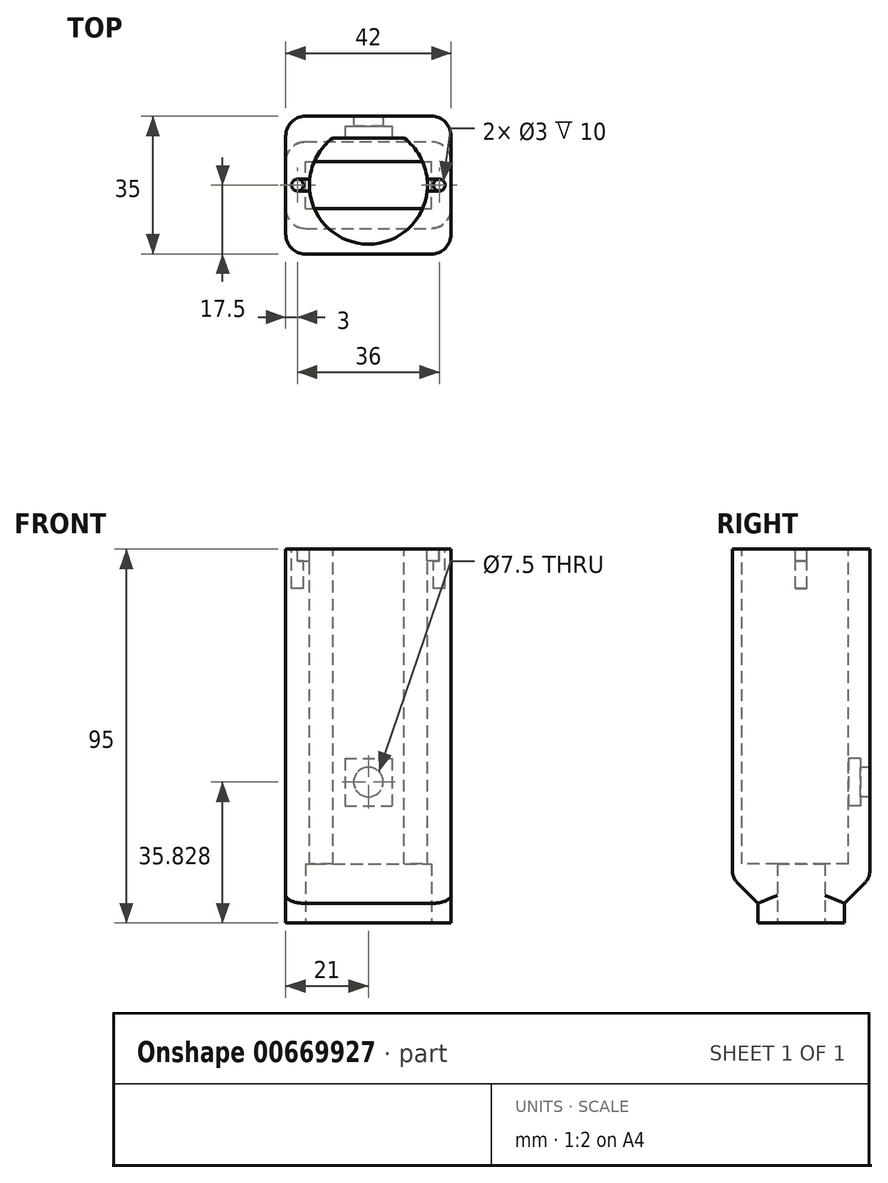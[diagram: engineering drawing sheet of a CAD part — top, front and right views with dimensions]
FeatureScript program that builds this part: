
annotation { "Feature Type Name" : "Feature", "Feature Type Description" : "" }
export const myFeature = defineFeature(function(context is Context, id is Id, definition is map)
    precondition{}
    {
        {
            var Q0;
            Q0=qCreatedBy(makeId("Top.planeOp"),FACE);
            var sketch = newSketch(context, id + "F0", { "sketchPlane" : qUnion([Q0])});
            skLineSegment(sketch, "E0.bottom", {"start": v(-21, 11) * mm, "end": v(21, 11) * mm});
            skLineSegment(sketch, "E0.top", {"start": v(-21, -11) * mm, "end": v(21, -11) * mm});
            skLineSegment(sketch, "E0.left", {"start": v(-21, 11) * mm, "end": v(-21, -11) * mm});
            skLineSegment(sketch, "E0.right", {"start": v(21, 11) * mm, "end": v(21, -11) * mm});
            skSolve(sketch);
        }
        {
            var Q0;
            Q0 = qSketchRegion(id + "F0", true);
            extrude(context, id + "F1", {"entities" : qUnion([Q0]), "oppositeDirection" : true, "depth" : 5 * mm, "offsetDistance" : 25 * mm});
        }
        {
            var Q0;
            Q0=qCreatedBy(makeId("Top.planeOp"),FACE);
            var sketch = newSketch(context, id + "F2", { "sketchPlane" : qUnion([Q0])});
            skLineSegment(sketch, "E1.bottom", {"start": v(-21, 17.5) * mm, "end": v(21, 17.5) * mm});
            skLineSegment(sketch, "E1.top", {"start": v(-21, -17.5) * mm, "end": v(21, -17.5) * mm});
            skLineSegment(sketch, "E1.left", {"start": v(-21, 17.5) * mm, "end": v(-21, -17.5) * mm});
            skLineSegment(sketch, "E1.right", {"start": v(21, 17.5) * mm, "end": v(21, -17.5) * mm});
            skSolve(sketch);
        }
        {
            var Q0;
            Q0 = qSketchRegion(id + "F2", true);
            extrude(context, id + "F3", {"entities" : qUnion([Q0]), "operationType" : NewBodyOperationType.ADD, "depth" : 90 * mm, "offsetDistance" : 25 * mm});
        }
        {
            var Q0;
            Q0=makeQuery(id+"F3.opExtrude","CAP_EDGE",EDGE,{"disambiguationData":[OSD([sQuery(id+"F2.wireOp",EDGE,"E1.top")])],"isStart":true});
            var Q1;
            Q1=makeQuery(id+"F3.opExtrude","CAP_EDGE",EDGE,{"disambiguationData":[OSD([sQuery(id+"F2.wireOp",EDGE,"E1.bottom")])],"isStart":true});
            chamfer(context, id + "F4", {"entities" : qUnion([Q0, Q1]), "width" : 6.5 * mm, "tangentPropagation" : true});
        }
        {
            var Q0;
            Q0=makeQuery(id+"F3.opExtrude","CAP_FACE",FACE,{"disambiguationData":[OSD([sQuery(id+"F2.wireOp",EDGE,"E1.bottom"),sQuery(id+"F2.wireOp",EDGE,"E1.top"),sQuery(id+"F2.wireOp",EDGE,"E1.left"),sQuery(id+"F2.wireOp",EDGE,"E1.right")])],"isStart":false});
            var sketch = newSketch(context, id + "F5", { "sketchPlane" : qUnion([Q0])});
            skCircle(sketch, "E2", {"center": v(0, 0) * mm, "radius": 15 * mm});
            skLineSegment(sketch, "E3", {"start": v(-9, 12) * mm, "end": v(9, 12) * mm});
            skSolve(sketch);
        }
        {
            var Q0;
            {var subQ0=sQuery(id+"F5.wireOp",EDGE,"E3");Q0=makeQuery(id+"F5.imprint","IMPRINT",FACE,{"disambiguationData":[TD([[makeQuery(id+"F5.imprint","IMPRINT",EDGE,{"derivedFrom":subQ0}),-1.0]])]});}
            extrude(context, id + "F6", {"entities" : qUnion([Q0]), "operationType" : NewBodyOperationType.REMOVE, "oppositeDirection" : true, "depth" : 80 * mm, "offsetDistance" : 25 * mm});
        }
        {
            var Q0;
            Q0=makeQuery(id+"F3.opExtrude","SWEPT_EDGE",EDGE,{"disambiguationData":[OSD([sQuery(id+"F2.wireOp",EDGE,"E1.top"),sQuery(id+"F2.wireOp",EDGE,"E1.right")])]});
            var Q1;
            Q1=makeQuery(id+"F4.opChamfer","BLEND_EDGE",EDGE,{"blendedFrom":[makeQuery(id+"F3.opExtrude","CAP_EDGE",EDGE,{"disambiguationData":[OSD([sQuery(id+"F2.wireOp",EDGE,"E1.top")])],"isStart":true}),makeQuery(id+"F3.boolean.opBoolean","MERGE",FACE,{"derivedFrom":[makeQuery(id+"F1.opExtrude","SWEPT_FACE",FACE,{"disambiguationData":[OSD([sQuery(id+"F0.wireOp",EDGE,"E0.right")])]}),makeQuery(id+"F3.opExtrude","SWEPT_FACE",FACE,{"disambiguationData":[OSD([sQuery(id+"F2.wireOp",EDGE,"E1.right")])]})]})],"blendedInto":[makeQuery(id+"F3.boolean.opBoolean","MERGE",FACE,{"derivedFrom":[makeQuery(id+"F1.opExtrude","SWEPT_FACE",FACE,{"disambiguationData":[OSD([sQuery(id+"F0.wireOp",EDGE,"E0.right")])]}),makeQuery(id+"F3.opExtrude","SWEPT_FACE",FACE,{"disambiguationData":[OSD([sQuery(id+"F2.wireOp",EDGE,"E1.right")])]})]})]});
            var Q2;
            Q2=makeQuery(id+"F1.opExtrude","SWEPT_EDGE",EDGE,{"disambiguationData":[OSD([sQuery(id+"F0.wireOp",EDGE,"E0.top"),sQuery(id+"F0.wireOp",EDGE,"E0.right")])]});
            var Q3;
            Q3=makeQuery(id+"F3.opExtrude","SWEPT_EDGE",EDGE,{"disambiguationData":[OSD([sQuery(id+"F2.wireOp",EDGE,"E1.top"),sQuery(id+"F2.wireOp",EDGE,"E1.left")])]});
            var Q4;
            Q4=makeQuery(id+"F4.opChamfer","BLEND_EDGE",EDGE,{"blendedFrom":[makeQuery(id+"F3.opExtrude","CAP_EDGE",EDGE,{"disambiguationData":[OSD([sQuery(id+"F2.wireOp",EDGE,"E1.top")])],"isStart":true}),makeQuery(id+"F3.boolean.opBoolean","MERGE",FACE,{"derivedFrom":[makeQuery(id+"F1.opExtrude","SWEPT_FACE",FACE,{"disambiguationData":[OSD([sQuery(id+"F0.wireOp",EDGE,"E0.left")])]}),makeQuery(id+"F3.opExtrude","SWEPT_FACE",FACE,{"disambiguationData":[OSD([sQuery(id+"F2.wireOp",EDGE,"E1.left")])]})]})],"blendedInto":[makeQuery(id+"F3.boolean.opBoolean","MERGE",FACE,{"derivedFrom":[makeQuery(id+"F1.opExtrude","SWEPT_FACE",FACE,{"disambiguationData":[OSD([sQuery(id+"F0.wireOp",EDGE,"E0.left")])]}),makeQuery(id+"F3.opExtrude","SWEPT_FACE",FACE,{"disambiguationData":[OSD([sQuery(id+"F2.wireOp",EDGE,"E1.left")])]})]})]});
            var Q5;
            Q5=makeQuery(id+"F1.opExtrude","SWEPT_EDGE",EDGE,{"disambiguationData":[OSD([sQuery(id+"F0.wireOp",EDGE,"E0.top"),sQuery(id+"F0.wireOp",EDGE,"E0.left")])]});
            var Q6;
            Q6=makeQuery(id+"F3.opExtrude","SWEPT_EDGE",EDGE,{"disambiguationData":[OSD([sQuery(id+"F2.wireOp",EDGE,"E1.bottom"),sQuery(id+"F2.wireOp",EDGE,"E1.left")])]});
            var Q7;
            Q7=makeQuery(id+"F4.opChamfer","BLEND_EDGE",EDGE,{"blendedFrom":[makeQuery(id+"F3.opExtrude","CAP_EDGE",EDGE,{"disambiguationData":[OSD([sQuery(id+"F2.wireOp",EDGE,"E1.bottom")])],"isStart":true}),makeQuery(id+"F3.boolean.opBoolean","MERGE",FACE,{"derivedFrom":[makeQuery(id+"F1.opExtrude","SWEPT_FACE",FACE,{"disambiguationData":[OSD([sQuery(id+"F0.wireOp",EDGE,"E0.left")])]}),makeQuery(id+"F3.opExtrude","SWEPT_FACE",FACE,{"disambiguationData":[OSD([sQuery(id+"F2.wireOp",EDGE,"E1.left")])]})]})],"blendedInto":[makeQuery(id+"F3.boolean.opBoolean","MERGE",FACE,{"derivedFrom":[makeQuery(id+"F1.opExtrude","SWEPT_FACE",FACE,{"disambiguationData":[OSD([sQuery(id+"F0.wireOp",EDGE,"E0.left")])]}),makeQuery(id+"F3.opExtrude","SWEPT_FACE",FACE,{"disambiguationData":[OSD([sQuery(id+"F2.wireOp",EDGE,"E1.left")])]})]})]});
            var Q8;
            Q8=makeQuery(id+"F1.opExtrude","SWEPT_EDGE",EDGE,{"disambiguationData":[OSD([sQuery(id+"F0.wireOp",EDGE,"E0.bottom"),sQuery(id+"F0.wireOp",EDGE,"E0.left")])]});
            var Q9;
            Q9=makeQuery(id+"F3.opExtrude","SWEPT_EDGE",EDGE,{"disambiguationData":[OSD([sQuery(id+"F2.wireOp",EDGE,"E1.bottom"),sQuery(id+"F2.wireOp",EDGE,"E1.right")])]});
            var Q10;
            Q10=makeQuery(id+"F4.opChamfer","BLEND_EDGE",EDGE,{"blendedFrom":[makeQuery(id+"F3.opExtrude","CAP_EDGE",EDGE,{"disambiguationData":[OSD([sQuery(id+"F2.wireOp",EDGE,"E1.bottom")])],"isStart":true}),makeQuery(id+"F3.boolean.opBoolean","MERGE",FACE,{"derivedFrom":[makeQuery(id+"F1.opExtrude","SWEPT_FACE",FACE,{"disambiguationData":[OSD([sQuery(id+"F0.wireOp",EDGE,"E0.right")])]}),makeQuery(id+"F3.opExtrude","SWEPT_FACE",FACE,{"disambiguationData":[OSD([sQuery(id+"F2.wireOp",EDGE,"E1.right")])]})]})],"blendedInto":[makeQuery(id+"F3.boolean.opBoolean","MERGE",FACE,{"derivedFrom":[makeQuery(id+"F1.opExtrude","SWEPT_FACE",FACE,{"disambiguationData":[OSD([sQuery(id+"F0.wireOp",EDGE,"E0.right")])]}),makeQuery(id+"F3.opExtrude","SWEPT_FACE",FACE,{"disambiguationData":[OSD([sQuery(id+"F2.wireOp",EDGE,"E1.right")])]})]})]});
            var Q11;
            Q11=makeQuery(id+"F1.opExtrude","SWEPT_EDGE",EDGE,{"disambiguationData":[OSD([sQuery(id+"F0.wireOp",EDGE,"E0.bottom"),sQuery(id+"F0.wireOp",EDGE,"E0.right")])]});
            var Q12;
            {var subQ0=sQuery(id+"F2.wireOp",EDGE,"E1.bottom");Q12=makeQuery(id+"F4.opChamfer","BLEND_EDGE",EDGE,{"blendedFrom":[makeQuery(id+"F3.opExtrude","CAP_EDGE",EDGE,{"disambiguationData":[OSD([subQ0])],"isStart":true}),makeQuery(id+"F3.opExtrude","SWEPT_FACE",FACE,{"disambiguationData":[OSD([subQ0])]})],"blendedInto":[makeQuery(id+"F3.opExtrude","SWEPT_FACE",FACE,{"disambiguationData":[OSD([subQ0])]})]});}
            var Q13;
            {var subQ0=sQuery(id+"F2.wireOp",EDGE,"E1.top");Q13=makeQuery(id+"F4.opChamfer","BLEND_EDGE",EDGE,{"blendedFrom":[makeQuery(id+"F3.opExtrude","CAP_EDGE",EDGE,{"disambiguationData":[OSD([subQ0])],"isStart":true}),makeQuery(id+"F3.opExtrude","SWEPT_FACE",FACE,{"disambiguationData":[OSD([subQ0])]})],"blendedInto":[makeQuery(id+"F3.opExtrude","SWEPT_FACE",FACE,{"disambiguationData":[OSD([subQ0])]})]});}
            fillet(context, id + "F7", {"entities" : qUnion([Q0, Q1, Q2, Q3, Q4, Q5, Q6, Q7, Q8, Q9, Q10, Q11, Q12, Q13]), "radius" : 5 * mm, "tangentPropagation" : true, "allowEdgeOverflow" : false});
        }
        {
            var Q0;
            Q0=makeQuery(id+"F1.opExtrude","CAP_FACE",FACE,{"disambiguationData":[OSD([sQuery(id+"F0.wireOp",EDGE,"E0.bottom"),sQuery(id+"F0.wireOp",EDGE,"E0.top"),sQuery(id+"F0.wireOp",EDGE,"E0.left"),sQuery(id+"F0.wireOp",EDGE,"E0.right")])],"isStart":false});
            var sketch = newSketch(context, id + "F8", { "sketchPlane" : qUnion([Q0])});
            skLineSegment(sketch, "E4.bottom", {"start": v(-16, 6) * mm, "end": v(16, 6) * mm});
            skLineSegment(sketch, "E4.top", {"start": v(-16, -6) * mm, "end": v(16, -6) * mm});
            skLineSegment(sketch, "E4.left", {"start": v(-16, 6) * mm, "end": v(-16, -6) * mm});
            skLineSegment(sketch, "E4.right", {"start": v(16, 6) * mm, "end": v(16, -6) * mm});
            skSolve(sketch);
        }
        {
            var Q0;
            Q0 = qSketchRegion(id + "F8", true);
            extrude(context, id + "F9", {"entities" : qUnion([Q0]), "operationType" : NewBodyOperationType.REMOVE, "oppositeDirection" : true, "depth" : 15 * mm, "offsetDistance" : 25 * mm});
        }
        {
            var Q0;
            Q0=makeQuery(id+"F6.boolean.opBoolean","COPY",FACE,{"derivedFrom":makeQuery(id+"F6.opExtrude","SWEPT_FACE",FACE,{"disambiguationData":[OSD([sQuery(id+"F5.wireOp",EDGE,"E3")])]})});
            var sketch = newSketch(context, id + "F10", { "sketchPlane" : qUnion([Q0])});
            skLineSegment(sketch, "E5.bottom", {"start": v(-6, 36.83) * mm, "end": v(6, 36.83) * mm});
            skLineSegment(sketch, "E5.top", {"start": v(-6, 24.83) * mm, "end": v(6, 24.83) * mm});
            skLineSegment(sketch, "E5.left", {"start": v(-6, 36.83) * mm, "end": v(-6, 24.83) * mm});
            skLineSegment(sketch, "E5.right", {"start": v(6, 36.83) * mm, "end": v(6, 24.83) * mm});
            skCircle(sketch, "E6", {"center": v(0, 30.83) * mm, "radius": 3.75 * mm});
            skSolve(sketch);
        }
        {
            var Q0;
            Q0 = qSketchRegion(id + "F10", true);
            extrude(context, id + "F11", {"entities" : qUnion([Q0]), "operationType" : NewBodyOperationType.REMOVE, "oppositeDirection" : true, "depth" : 3 * mm, "offsetDistance" : 25 * mm});
        }
        {
            var Q0;
            Q0=makeQuery(id+"F11.boolean.opBoolean","SPLIT",FACE,{"disambiguationData":[TD([makeQuery(id+"F11.opExtrude","SWEPT_FACE",FACE,{"disambiguationData":[OSD([sQuery(id+"F10.wireOp",EDGE,"E6")])]})])],"derivedFrom":makeQuery(id+"F6.boolean.opBoolean","COPY",FACE,{"derivedFrom":makeQuery(id+"F6.opExtrude","SWEPT_FACE",FACE,{"disambiguationData":[OSD([sQuery(id+"F5.wireOp",EDGE,"E3")])]})})});
            extrude(context, id + "F12", {"entities" : qUnion([Q0]), "operationType" : NewBodyOperationType.REMOVE, "oppositeDirection" : true, "depth" : 10 * mm, "offsetDistance" : 25 * mm});
        }
        {
            var Q0;
            Q0=makeQuery(id+"F3.opExtrude","CAP_FACE",FACE,{"disambiguationData":[OSD([sQuery(id+"F2.wireOp",EDGE,"E1.bottom"),sQuery(id+"F2.wireOp",EDGE,"E1.top"),sQuery(id+"F2.wireOp",EDGE,"E1.left"),sQuery(id+"F2.wireOp",EDGE,"E1.right")])],"isStart":false});
            var sketch = newSketch(context, id + "F13", { "sketchPlane" : qUnion([Q0])});
            skCircle(sketch, "E7", {"center": v(-18, 0) * mm, "radius": 1.5 * mm});
            skCircle(sketch, "E8", {"center": v(18, 0) * mm, "radius": 1.5 * mm});
            skSolve(sketch);
        }
        {
            var Q0;
            Q0 = qSketchRegion(id + "F13", true);
            extrude(context, id + "F14", {"entities" : qUnion([Q0]), "operationType" : NewBodyOperationType.REMOVE, "oppositeDirection" : true, "depth" : 10 * mm, "offsetDistance" : 25 * mm});
        }
        {
            var Q0;
            Q0=makeQuery(id+"F3.opExtrude","CAP_FACE",FACE,{"disambiguationData":[OSD([sQuery(id+"F2.wireOp",EDGE,"E1.bottom"),sQuery(id+"F2.wireOp",EDGE,"E1.top"),sQuery(id+"F2.wireOp",EDGE,"E1.left"),sQuery(id+"F2.wireOp",EDGE,"E1.right")])],"isStart":false});
            var sketch = newSketch(context, id + "F15", { "sketchPlane" : qUnion([Q0])});
            skLineSegment(sketch, "E9.bottom", {"start": v(-17.95, 1.5) * mm, "end": v(-14.92, 1.5) * mm});
            skLineSegment(sketch, "E9.top", {"start": v(-17.95, -1.5) * mm, "end": v(-14.92, -1.5) * mm});
            skLineSegment(sketch, "E9.left", {"start": v(-17.95, 1.5) * mm, "end": v(-17.95, -1.5) * mm});
            skLineSegment(sketch, "E9.right", {"start": v(-14.92, 1.5) * mm, "end": v(-14.92, -1.5) * mm});
            skLineSegment(sketch, "E10.bottom", {"start": v(18.1, 1.5) * mm, "end": v(14.92, 1.5) * mm});
            skLineSegment(sketch, "E10.top", {"start": v(18.1, -1.5) * mm, "end": v(14.92, -1.5) * mm});
            skLineSegment(sketch, "E10.left", {"start": v(18.1, 1.5) * mm, "end": v(18.1, -1.5) * mm});
            skLineSegment(sketch, "E10.right", {"start": v(14.92, 1.5) * mm, "end": v(14.92, -1.5) * mm});
            skSolve(sketch);
        }
        {
            var Q0;
            Q0 = qSketchRegion(id + "F15", true);
            extrude(context, id + "F16", {"entities" : qUnion([Q0]), "operationType" : NewBodyOperationType.REMOVE, "oppositeDirection" : true, "depth" : 3 * mm, "offsetDistance" : 25 * mm});
        }
    });
